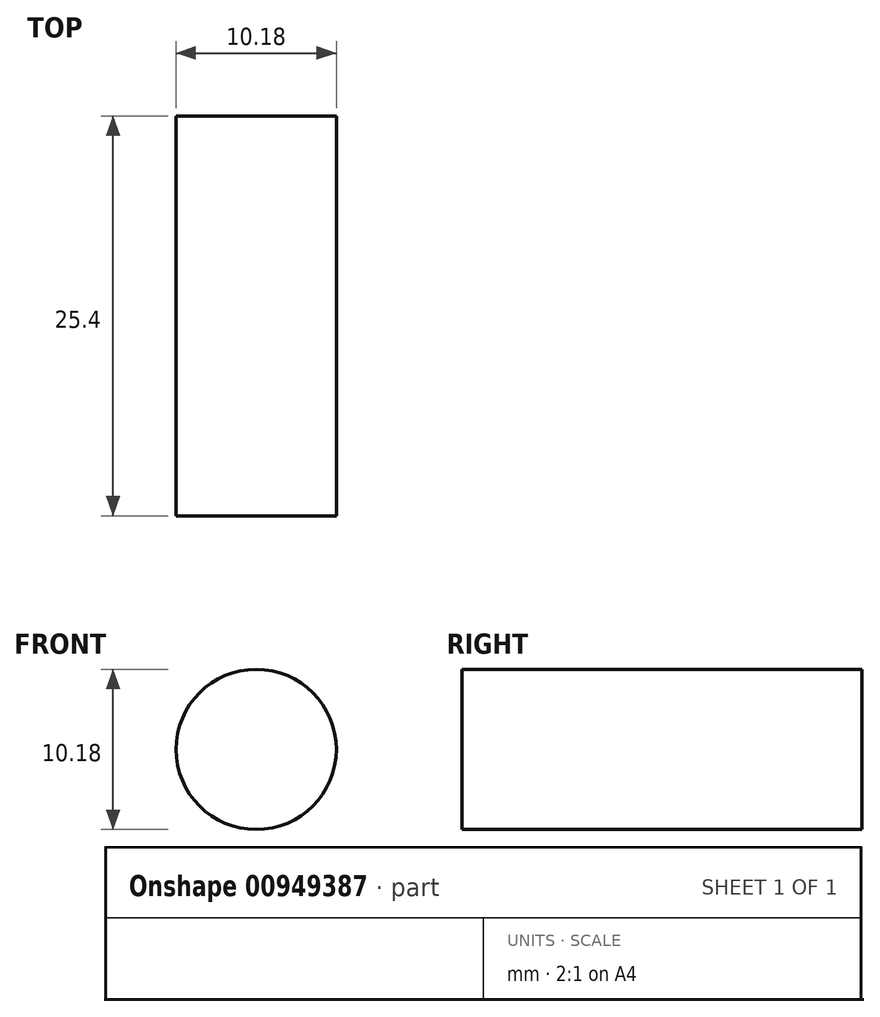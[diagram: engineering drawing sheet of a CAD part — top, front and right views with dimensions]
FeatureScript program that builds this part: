
annotation { "Feature Type Name" : "Feature", "Feature Type Description" : "" }
export const myFeature = defineFeature(function(context is Context, id is Id, definition is map)
    precondition{}
    {
        {
            var Q0;
            Q0=qCreatedBy(makeId("Front.planeOp"),FACE);
            var sketch = newSketch(context, id + "F0", { "sketchPlane" : qUnion([Q0])});
            skCircle(sketch, "E0", {"center": v(0, 0) * mm, "radius": 5.09 * mm});
            skSolve(sketch);
        }
        {
            var Q0;
            Q0=qSketchRegion(id+"F0",true);
            extrude(context, id + "F1", {"entities" : qUnion([Q0]), "depth" : 25.4 * mm, "offsetDistance" : 25.4 * mm});
        }
    });
